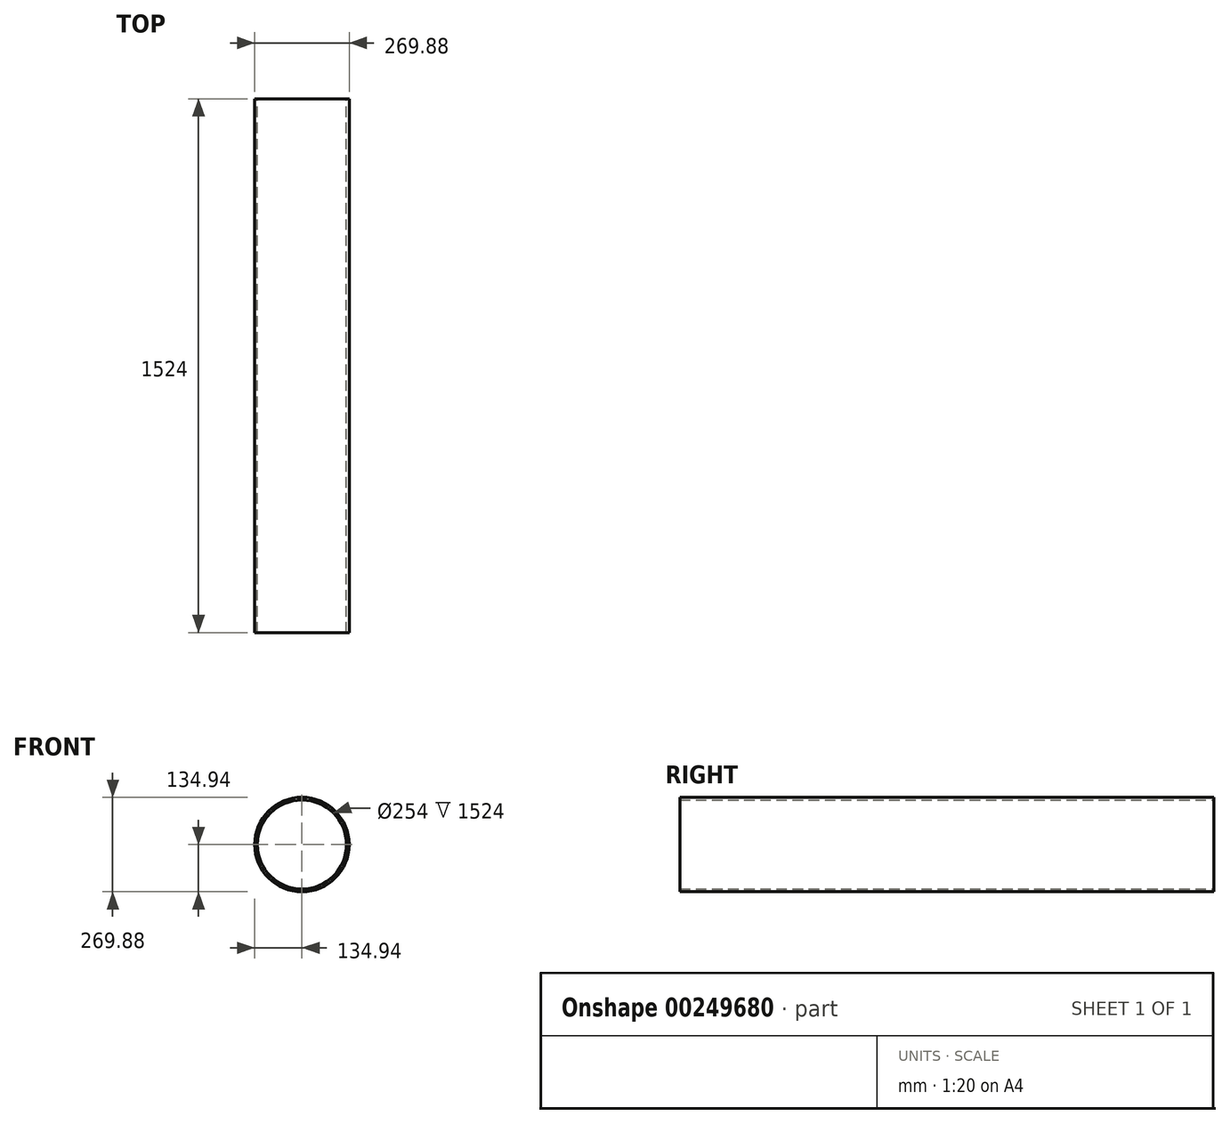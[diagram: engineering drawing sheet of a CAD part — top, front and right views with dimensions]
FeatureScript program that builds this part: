
annotation { "Feature Type Name" : "Feature", "Feature Type Description" : "" }
export const myFeature = defineFeature(function(context is Context, id is Id, definition is map)
    precondition{}
    {
        {
            var Q0;
            Q0=qCreatedBy(makeId("Front.planeOp"),FACE);
            var sketch = newSketch(context, id + "F0", { "sketchPlane" : qUnion([Q0])});
            skCircle(sketch, "E0", {"center": v(0, 0) * mm, "radius": 127 * mm});
            skCircle(sketch, "E1", {"center": v(0, 0) * mm, "radius": 134.94 * mm});
            skSolve(sketch);
        }
        {
            var Q0;
            Q0 = qSketchRegion(id + "F0", true);
            extrude(context, id + "F1", {"entities" : qUnion([Q0]), "endBound" : BoundingType.SYMMETRIC, "depth" : 1524 * mm});
        }
    });
